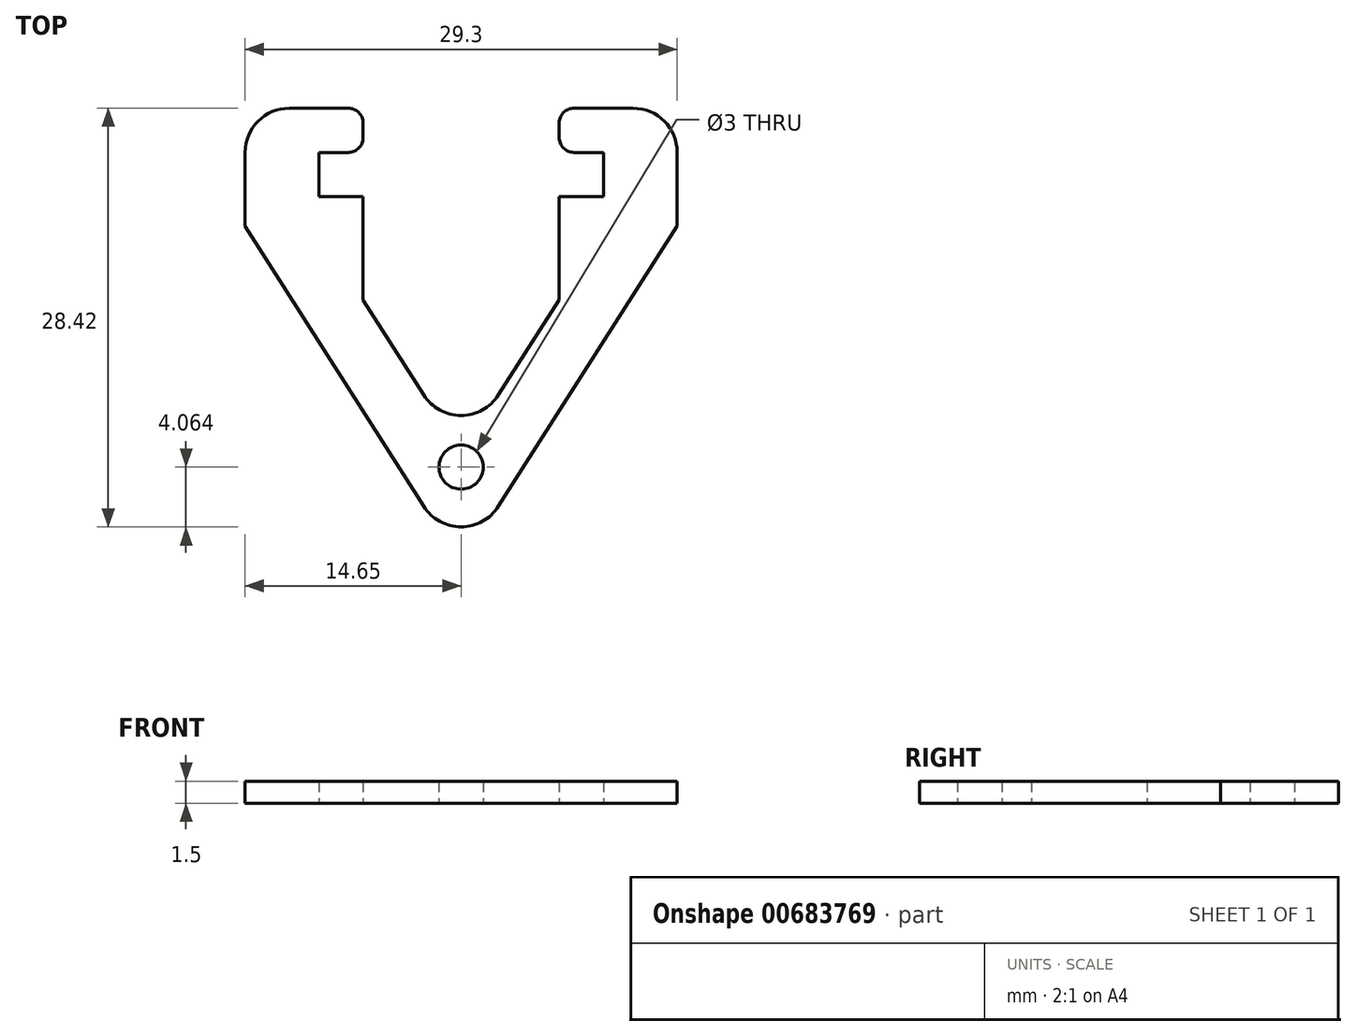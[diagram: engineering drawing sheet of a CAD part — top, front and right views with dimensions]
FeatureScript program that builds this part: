
annotation { "Feature Type Name" : "Feature", "Feature Type Description" : "" }
export const myFeature = defineFeature(function(context is Context, id is Id, definition is map)
    precondition{}
    {
        {
            assignVariable(context, id + "F0", {"name" : "thick", "anyValue" : 1.5});
        }
        {
            var Q0;
            Q0=qCreatedBy(makeId("Top.planeOp"),FACE);
            var sketch = newSketch(context, id + "F1", { "sketchPlane" : qUnion([Q0])});
            skLineSegment(sketch, "E0", {"start": v(-2.53, 3.97) * mm, "end": v(-14.65, 23) * mm});
            skLineSegment(sketch, "E1", {"start": v(14.65, 23) * mm, "end": v(2.53, 3.97) * mm});
            skLineSegment(sketch, "E2", {"start": v(0, 0) * mm, "end": v(0, 23) * mm, "construction": true});
            skLineSegment(sketch, "E3", {"start": v(-6.65, 23) * mm, "end": v(-14.65, 23) * mm, "construction": true});
            skLineSegment(sketch, "E4", {"start": v(6.65, 23) * mm, "end": v(14.65, 23) * mm, "construction": true});
            skLineSegment(sketch, "E5", {"start": v(-14.65, 23) * mm, "end": v(-14.65, 28) * mm});
            skLineSegment(sketch, "E6", {"start": v(-11.65, 31) * mm, "end": v(-7.65, 31) * mm});
            skLineSegment(sketch, "E7", {"start": v(14.65, 28) * mm, "end": v(14.65, 23) * mm});
            skLineSegment(sketch, "E8", {"start": v(-7.65, 28) * mm, "end": v(-9.65, 28) * mm});
            skLineSegment(sketch, "E9", {"start": v(-9.65, 28) * mm, "end": v(-9.65, 25) * mm});
            skLineSegment(sketch, "E10", {"start": v(-9.65, 25) * mm, "end": v(-6.65, 25) * mm});
            skLineSegment(sketch, "E11", {"start": v(-6.65, 29) * mm, "end": v(-6.65, 30) * mm});
            skLineSegment(sketch, "E12", {"start": v(-6.65, 25) * mm, "end": v(-6.65, 18) * mm});
            skLineSegment(sketch, "E13.MirrorCS", {"start": v(6.65, 25) * mm, "end": v(6.65, 18) * mm});
            skLineSegment(sketch, "E14.MirrorCS", {"start": v(9.65, 25) * mm, "end": v(6.65, 25) * mm});
            skLineSegment(sketch, "E15.MirrorCS", {"start": v(9.65, 28) * mm, "end": v(9.65, 25) * mm});
            skLineSegment(sketch, "E16.MirrorCS", {"start": v(7.65, 28) * mm, "end": v(9.65, 28) * mm});
            skLineSegment(sketch, "E17.MirrorCS", {"start": v(6.65, 29) * mm, "end": v(6.65, 30) * mm});
            skLineSegment(sketch, "E18", {"start": v(-6.65, 18) * mm, "end": v(-2.53, 11.53) * mm});
            skLineSegment(sketch, "E19.MirrorCS", {"start": v(6.65, 18) * mm, "end": v(2.53, 11.53) * mm});
            skPoint(sketch, "E20.visualSharp", {"position": v(-14.65, 31) * mm});
            skArc(sketch, "E20.filletArc", {"start": v(-11.65, 31) * mm, "mid": v(-13.77, 30.12) * mm, "end": v(-14.65, 28) * mm});
            skPoint(sketch, "E21.visualSharp", {"position": v(14.65, 31) * mm});
            skArc(sketch, "E21.filletArc", {"start": v(14.65, 28) * mm, "mid": v(13.77, 30.12) * mm, "end": v(11.65, 31) * mm});
            skPoint(sketch, "E22.visualSharp", {"position": v(0, 7.56) * mm});
            skArc(sketch, "E22.filletArc", {"start": v(-2.53, 11.53) * mm, "mid": v(0, 10.14) * mm, "end": v(2.53, 11.53) * mm});
            skPoint(sketch, "E23.visualSharp", {"position": v(0, 0) * mm});
            skArc(sketch, "E23.filletArc", {"start": v(-2.53, 3.97) * mm, "mid": v(0, 2.58) * mm, "end": v(2.53, 3.97) * mm});
            skCircle(sketch, "E24", {"center": v(0, 6.64) * mm, "radius": 1.5 * mm});
            skLineSegment(sketch, "E25.trimOffspring", {"start": v(7.65, 31) * mm, "end": v(11.65, 31) * mm});
            skPoint(sketch, "E26.visualSharp", {"position": v(-6.65, 31) * mm});
            skArc(sketch, "E26.filletArc", {"start": v(-6.65, 30) * mm, "mid": v(-6.94, 30.7) * mm, "end": v(-7.65, 31) * mm});
            skPoint(sketch, "E27.visualSharp", {"position": v(-6.65, 28) * mm});
            skArc(sketch, "E27.filletArc", {"start": v(-7.65, 28) * mm, "mid": v(-6.94, 28.3) * mm, "end": v(-6.65, 29) * mm});
            skPoint(sketch, "E28.visualSharp", {"position": v(6.65, 31) * mm});
            skArc(sketch, "E28.filletArc", {"start": v(7.65, 31) * mm, "mid": v(6.94, 30.7) * mm, "end": v(6.65, 30) * mm});
            skPoint(sketch, "E29.visualSharp", {"position": v(6.65, 28) * mm});
            skArc(sketch, "E29.filletArc", {"start": v(6.65, 29) * mm, "mid": v(6.94, 28.3) * mm, "end": v(7.65, 28) * mm});
            skSolve(sketch);
        }
        {
            var Q0;
            Q0=makeQuery(id+"F1.imprint","IMPRINT",FACE,{"disambiguationData":[TD([[makeQuery(id+"F1.imprint","IMPRINT",EDGE,{"derivedFrom":sQuery(id+"F1.wireOp",EDGE,"E0")}),-1.0]])]});
            extrude(context, id + "F2", {"entities" : qUnion([Q0]), "depth" : (getVariable(context, 'thick')) * mm, "offsetDistance" : 25 * mm});
        }
    });
